# Revit family: rba-bim-rba7742-777-005
name_source: partatom
category: Specialty Equipment
revit_build: Autodesk Revit 2018 (Build: 20170223_1515(x64)
units: mm (PartAtom-declared; Revit-internal decimal feet)

## family parameters
Cut with Voids When Loaded = No
Host = Face
OmniClass Number = 23.40.20.21
OmniClass Title = Toilet and Bath Specialties
Part Type = Normal
Room Calculation Point = No
Round Connector Dimension = Use Diameter
Shared = No

## types (1)
- RBA7742-777-005
    ADA Compliant = Yes
    Assembly Code = C1030200
    Default Elevation = 0.762
    Description = Matte Black Surface-Mounted Waste Receptacle, 24L
    Manufacturer = RBA Group
    Materials and Finishes = Satin Stainless Steel, Matte Black
    Model = RBA7742-777-005
    Modified Issue = 20210712.01
    Product Name = Surface-Mounted Waste Receptacle
    Type Comments = Satin Finish
    URL = www.rba.com.au

## geometry (parser evidence)
native form markers: Blend x6, Sweep x2
no freeform markers — native parametric forms only
